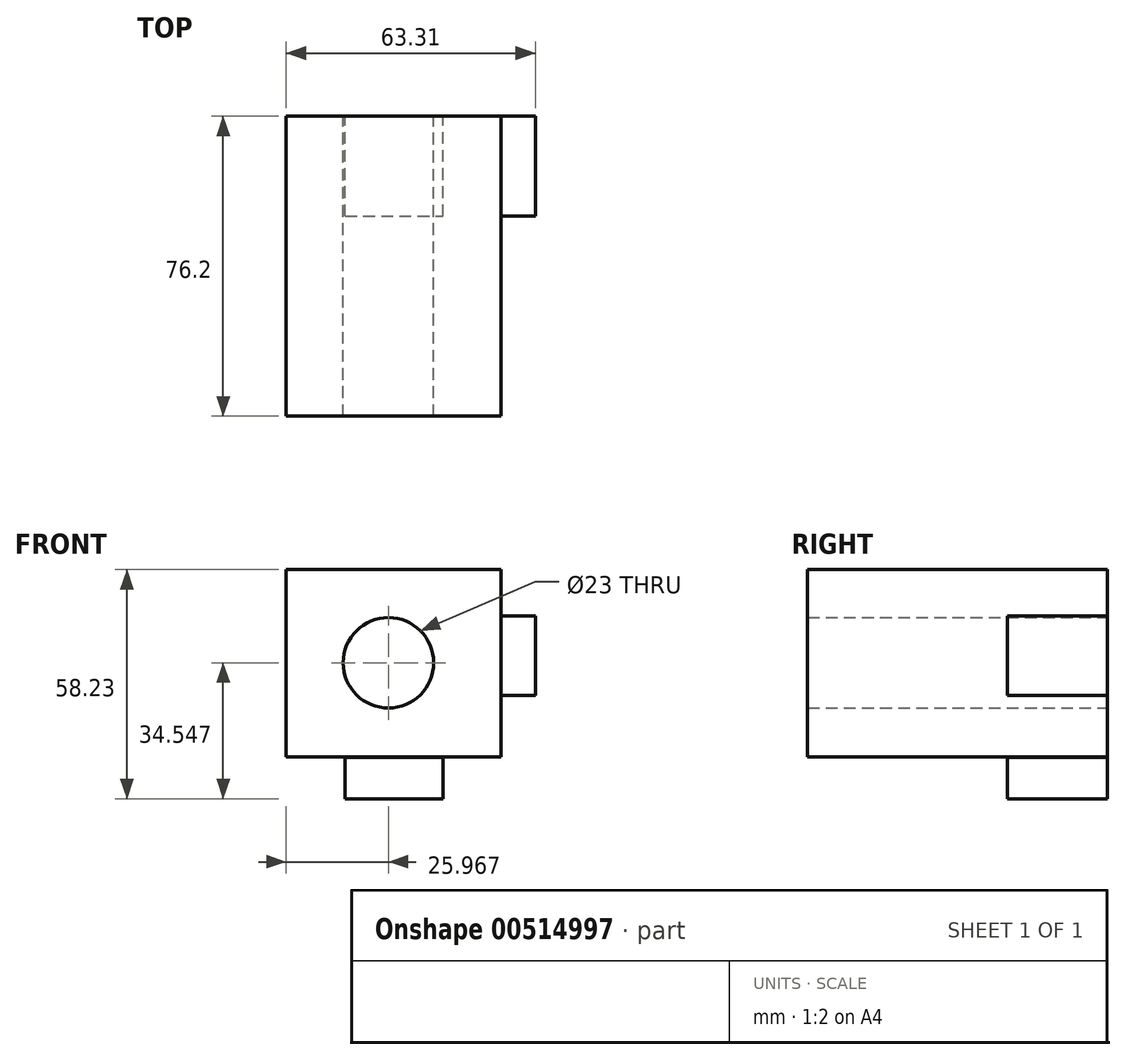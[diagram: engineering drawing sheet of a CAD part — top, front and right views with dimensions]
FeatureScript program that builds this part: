
annotation { "Feature Type Name" : "Feature", "Feature Type Description" : "" }
export const myFeature = defineFeature(function(context is Context, id is Id, definition is map)
    precondition{}
    {
        {
            var Q0;
            Q0=qCreatedBy(makeId("Front.planeOp"),FACE);
            var sketch = newSketch(context, id + "F0", { "sketchPlane" : qUnion([Q0])});
            skLineSegment(sketch, "E0.bottom", {"start": v(-54.61, 51.18) * mm, "end": v(0, 51.18) * mm});
            skLineSegment(sketch, "E0.top", {"start": v(-54.61, 3.63) * mm, "end": v(0, 3.63) * mm});
            skLineSegment(sketch, "E0.left", {"start": v(-54.61, 51.18) * mm, "end": v(-54.61, 3.63) * mm});
            skLineSegment(sketch, "E0.right", {"start": v(0, 51.18) * mm, "end": v(0, 3.63) * mm});
            skCircle(sketch, "E1", {"center": v(-28.64, 27.5) * mm, "radius": 11.5 * mm});
            skSolve(sketch);
        }
        {
            var Q0;
            Q0=qCreatedBy(makeId("Front.planeOp"),FACE);
            var sketch = newSketch(context, id + "F1", { "sketchPlane" : qUnion([Q0])});
            skLineSegment(sketch, "E2.bottom", {"start": v(-39.64, 3.48) * mm, "end": v(-14.8, 3.48) * mm});
            skLineSegment(sketch, "E2.top", {"start": v(-39.64, -7.05) * mm, "end": v(-14.8, -7.05) * mm});
            skLineSegment(sketch, "E2.left", {"start": v(-39.64, 3.48) * mm, "end": v(-39.64, -7.05) * mm});
            skLineSegment(sketch, "E2.right", {"start": v(-14.8, 3.48) * mm, "end": v(-14.8, -7.05) * mm});
            skLineSegment(sketch, "E3.bottom", {"start": v(0, 39.4) * mm, "end": v(8.7, 39.4) * mm});
            skLineSegment(sketch, "E3.top", {"start": v(0, 19.15) * mm, "end": v(8.7, 19.15) * mm});
            skLineSegment(sketch, "E3.left", {"start": v(0, 39.4) * mm, "end": v(0, 19.15) * mm});
            skLineSegment(sketch, "E3.right", {"start": v(8.7, 39.4) * mm, "end": v(8.7, 19.15) * mm});
            skSolve(sketch);
        }
        {
            var Q0;
            Q0=makeQuery(id+"F1.imprint","IMPRINT",FACE,{"disambiguationData":[TD([[makeQuery(id+"F1.imprint","IMPRINT",EDGE,{"derivedFrom":sQuery(id+"F1.wireOp",EDGE,"E3.bottom")}),-1.0]])]});
            var Q1;
            Q1=makeQuery(id+"F1.imprint","IMPRINT",FACE,{"disambiguationData":[TD([[makeQuery(id+"F1.imprint","IMPRINT",EDGE,{"derivedFrom":sQuery(id+"F1.wireOp",EDGE,"E2.bottom")}),-1.0]])]});
            var Q2;
            Q2=makeQuery(id+"F0.imprint","IMPRINT",FACE,{"disambiguationData":[TD([[makeQuery(id+"F0.imprint","IMPRINT",EDGE,{"derivedFrom":sQuery(id+"F0.wireOp",EDGE,"E0.bottom")}),-1.0]])]});
            extrude(context, id + "F2", {"entities" : qUnion([Q0, Q1, Q2]), "depth" : 25.4 * mm, "offsetDistance" : 25.4 * mm});
        }
        {
            var Q0;
            Q0=makeQuery(id+"F2.opExtrude","CAP_FACE",FACE,{"disambiguationData":[OSD([sQuery(id+"F0.wireOp",EDGE,"E0.bottom"),sQuery(id+"F0.wireOp",EDGE,"E0.top"),sQuery(id+"F0.wireOp",EDGE,"E0.left"),sQuery(id+"F0.wireOp",EDGE,"E0.right"),sQuery(id+"F0.wireOp",EDGE,"E1")])],"isStart":false});
            extrude(context, id + "F3", {"entities" : qUnion([Q0]), "operationType" : NewBodyOperationType.ADD, "depth" : 50.8 * mm, "offsetDistance" : 25.4 * mm});
        }
    });
